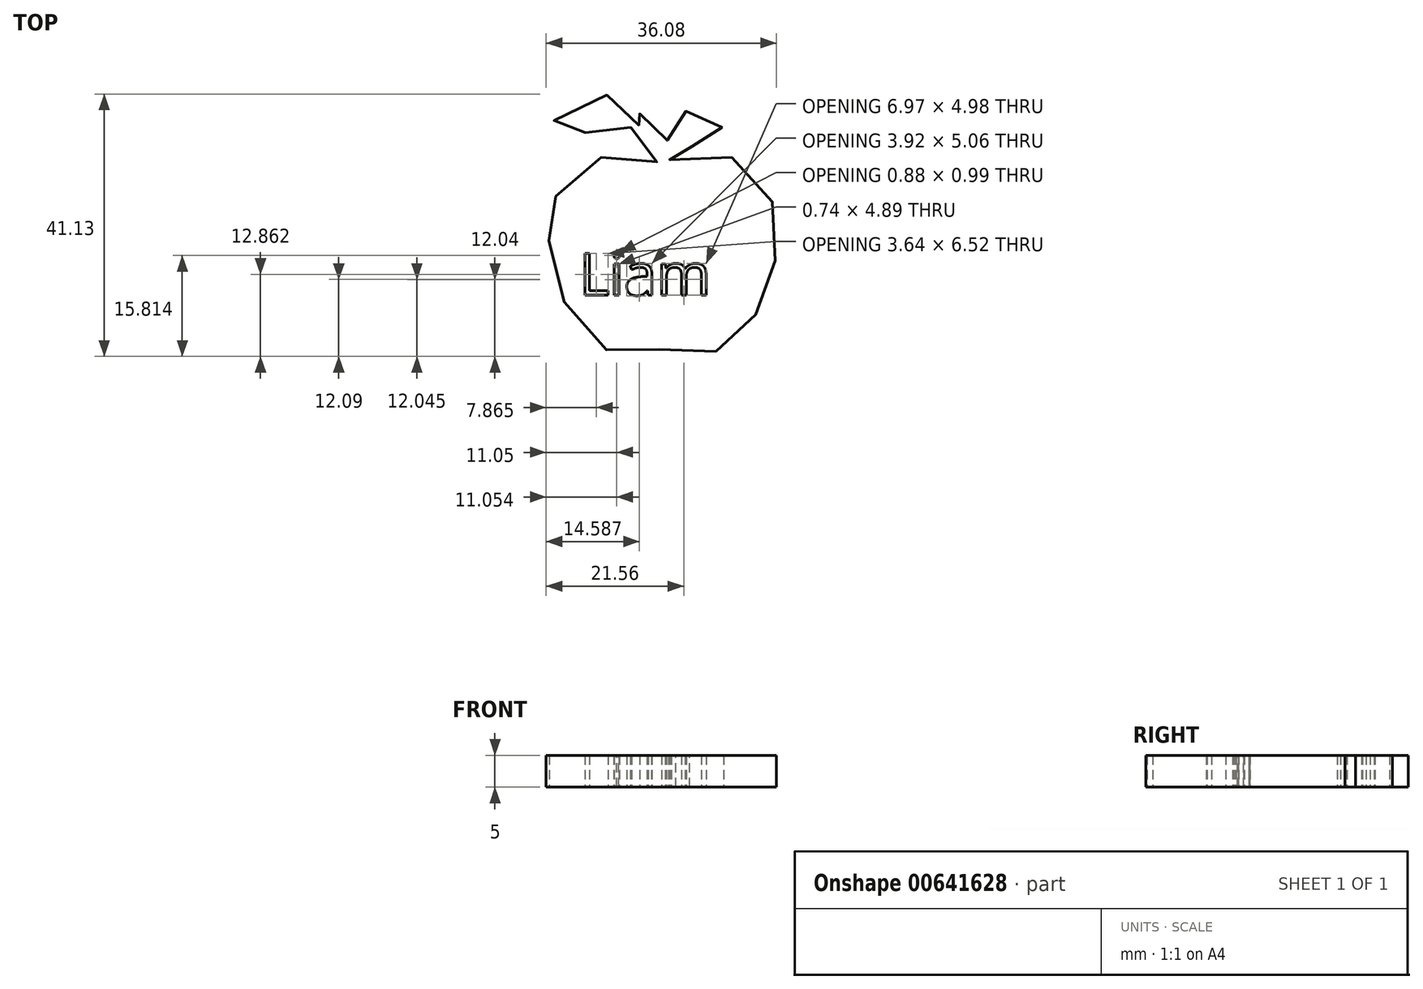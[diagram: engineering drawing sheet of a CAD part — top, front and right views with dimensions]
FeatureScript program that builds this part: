
annotation { "Feature Type Name" : "Feature", "Feature Type Description" : "" }
export const myFeature = defineFeature(function(context is Context, id is Id, definition is map)
    precondition{}
    {
        {
            var Q0;
            Q0=qCreatedBy(makeId("Top.planeOp"),FACE);
            var sketch = newSketch(context, id + "F0", { "sketchPlane" : qUnion([Q0])});
            skPoint(sketch, "E0.31.internal.snap0", {"position": v(-44.45, 9.07) * mm});
            skPoint(sketch, "E0.33.internal.snap0", {"position": v(-44.45, 9.07) * mm});
            skPoint(sketch, "E0.34.internal.snap0", {"position": v(-44.45, 9.07) * mm});
            skFitSpline(sketch, "E0", {"points": [v(-60.3, 30.14) * mm, v(-59.23, 24.98) * mm, v(-57.45, 19.65) * mm, v(-53.9, 15.02) * mm, v(-49.63, 12.36) * mm, v(-45.9, 12.53) * mm, v(-41.8, 13.07) * mm, v(-37.18, 12) * mm, v(-32.92, 13.42) * mm, v(-29.72, 15.74) * mm, v(-27.4, 19.47) * mm, v(-25.63, 23.56) * mm, v(-24.74, 28.18) * mm, v(-24.74, 32.98) * mm, v(-25.8, 37.78) * mm, v(-29.18, 42.4) * mm, v(-35.05, 42.94) * mm, v(-40.92, 42.23) * mm, v(-41.45, 44.54) * mm, v(-40.56, 45.78) * mm, v(-38.43, 44.9) * mm, v(-37.18, 45.25) * mm, v(-35.76, 46.5) * mm, v(-34.16, 47.74) * mm, v(-32.92, 48.1) * mm, v(-34.16, 49.7) * mm, v(-37.54, 50.59) * mm, v(-41.27, 49.16) * mm, v(-41.1, 46.85) * mm, v(-41.63, 45.78) * mm, v(-42.7, 47.74) * mm, v(-44.45, 49.87) * mm, v(-46.07, 50.05) * mm, v(-44.45, 47.56) * mm, v(-44.45, 46.5) * mm, v(-46.43, 48.63) * mm, v(-46.96, 50.58) * mm, v(-49.1, 52.36) * mm, v(-55.14, 52.9) * mm, v(-58.7, 50.05) * mm, v(-60.12, 47.2) * mm, v(-56.39, 47.74) * mm, v(-53.19, 46.32) * mm, v(-49.1, 46.5) * mm, v(-47.32, 47.92) * mm, v(-43.05, 44.36) * mm, v(-42.87, 42.58) * mm, v(-45.9, 43.12) * mm, v(-50.34, 43.47) * mm, v(-54.79, 42.23) * mm, v(-58.34, 38.67) * mm, v(-60.65, 33.16) * mm, v(-60.65, 32.1) * mm, v(-60.3, 30.14) * mm]});
            skText(sketch, "E1", { "text": "Liam", "fontName": "OpenSans-Regular.ttf"});
            const initialGuessF0  = {"E1": [-0.05556, 0.0216, 1, 0, 0.00658]};
            skSetInitialGuess(sketch, initialGuessF0);
            skSolve(sketch);
        }
        {
            var Q0;
            Q0=makeQuery(id+"F0.imprint","IMPRINT",FACE,{"disambiguationData":[TD([[makeQuery(id+"F0.imprint","IMPRINT",EDGE,{"derivedFrom":sQuery(id+"F0.wireOp",EDGE,"E0")}),1.0]])]});
            extrude(context, id + "F1", {"entities" : qUnion([Q0]), "depth" : 5 * mm, "offsetDistance" : 25.4 * mm});
        }
    });
